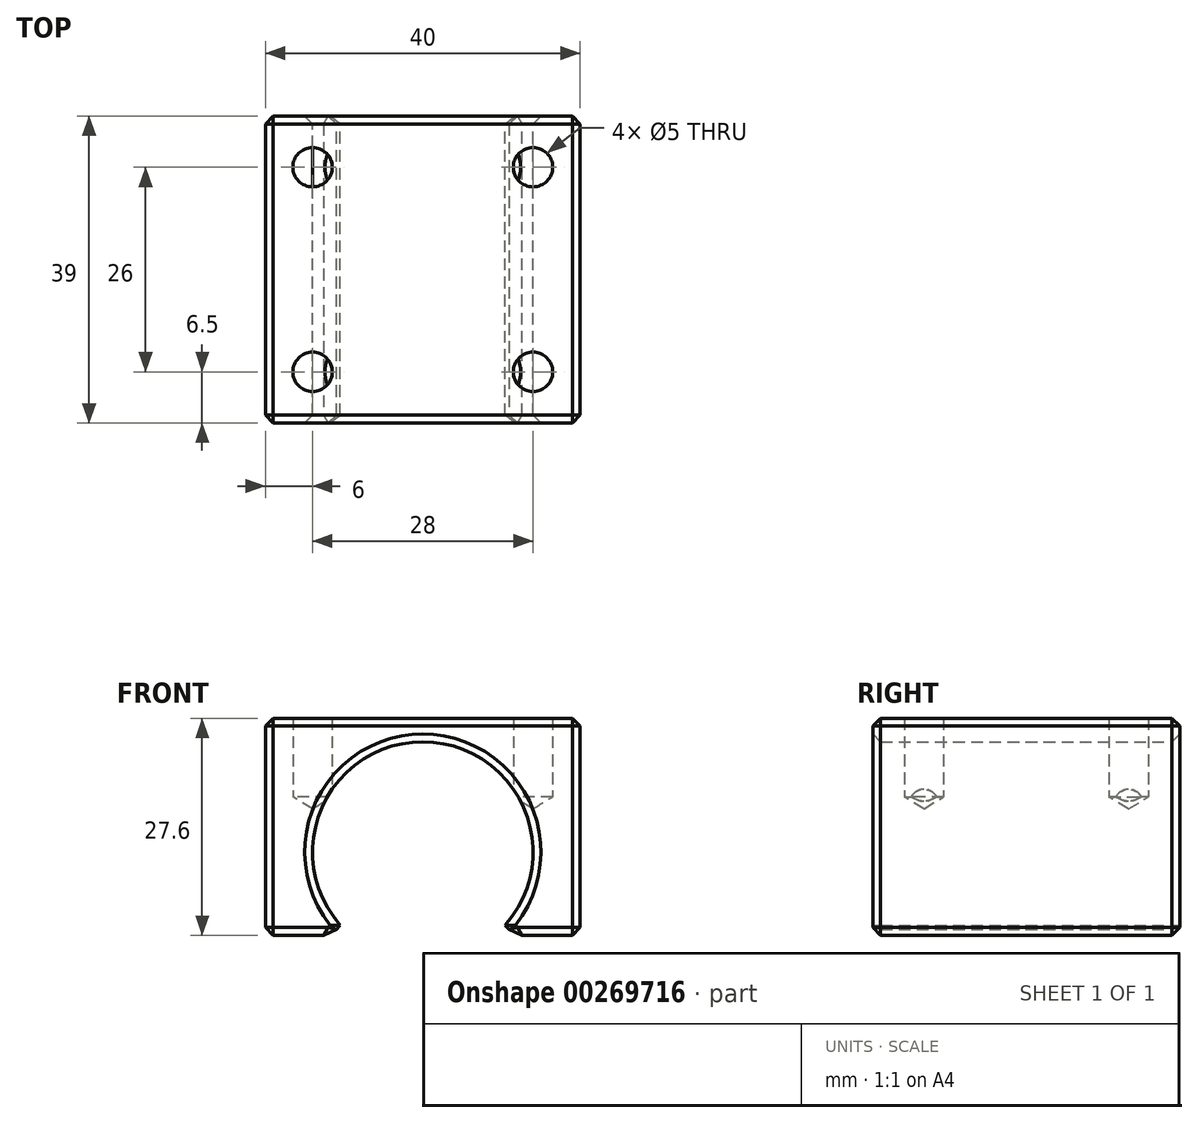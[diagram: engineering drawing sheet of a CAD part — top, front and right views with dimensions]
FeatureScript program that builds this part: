
annotation { "Feature Type Name" : "Feature", "Feature Type Description" : "" }
export const myFeature = defineFeature(function(context is Context, id is Id, definition is map)
    precondition{}
    {
        {
            var Q0;
            Q0=qCreatedBy(makeId("Front.planeOp"),FACE);
            var sketch = newSketch(context, id + "F0", { "sketchPlane" : qUnion([Q0])});
            skLineSegment(sketch, "E0.bottom", {"start": v(20, 13.8) * mm, "end": v(-20, 13.8) * mm});
            skLineSegment(sketch, "E0.top", {"start": v(20, -13.8) * mm, "end": v(11.58, -13.8) * mm});
            skLineSegment(sketch, "E0.left", {"start": v(20, 13.8) * mm, "end": v(20, -13.8) * mm});
            skLineSegment(sketch, "E0.right", {"start": v(-20, 13.8) * mm, "end": v(-20, -13.8) * mm});
            skPoint(sketch, "E0.middle", {"position": v(0, 0) * mm});
            skArc(sketch, "E1", {"start": v(10.48, -12.49) * mm, "mid": v(0, 10.8) * mm, "end": v(-10.48, -12.49) * mm});
            skLineSegment(sketch, "E2", {"start": v(-11.58, -13.8) * mm, "end": v(-10.48, -12.49) * mm});
            skLineSegment(sketch, "E3", {"start": v(11.58, -13.8) * mm, "end": v(10.48, -12.49) * mm});
            skLineSegment(sketch, "E4.trimOffspring", {"start": v(-11.58, -13.8) * mm, "end": v(-20, -13.8) * mm});
            skSolve(sketch);
        }
        {
            var Q0;
            Q0=makeQuery(id+"F0.imprint","IMPRINT",FACE,{"disambiguationData":[TD([[makeQuery(id+"F0.imprint","IMPRINT",EDGE,{"derivedFrom":sQuery(id+"F0.wireOp",EDGE,"E0.bottom")}),1.0]])]});
            extrude(context, id + "F1", {"entities" : qUnion([Q0]), "depth" : 39 * mm});
        }
        {
            var Q0;
            Q0=makeQuery(id+"F1.opExtrude","SWEPT_FACE",FACE,{"disambiguationData":[OSD([sQuery(id+"F0.wireOp",EDGE,"E0.bottom")])]});
            var sketch = newSketch(context, id + "F2", { "sketchPlane" : qUnion([Q0])});
            skPoint(sketch, "E5", {"position": v(-14, -6.5) * mm});
            skPoint(sketch, "E6", {"position": v(-14, -32.5) * mm});
            skPoint(sketch, "E7", {"position": v(14, -32.5) * mm});
            skPoint(sketch, "E8", {"position": v(14, -6.5) * mm});
            skLineSegment(sketch, "E9", {"start": v(-20, -19.5) * mm, "end": v(20, -19.5) * mm, "construction": true});
            skSolve(sketch);
        }
        {
            var Q0;
            Q0=sQuery(id+"F2.wireOp",VERTEX,"E5");
            var Q1;
            Q1=sQuery(id+"F2.wireOp",VERTEX,"E8");
            var Q2;
            Q2=sQuery(id+"F2.wireOp",VERTEX,"E7");
            var Q3;
            Q3=sQuery(id+"F2.wireOp",VERTEX,"E6");
            var Q4;
            Q4=makeQuery(id+"F1.opExtrude","SWEPT_BODY",BODY,{"disambiguationData":[OSD([sQuery(id+"F0.wireOp",EDGE,"E0.bottom"),sQuery(id+"F0.wireOp",EDGE,"E0.top"),sQuery(id+"F0.wireOp",EDGE,"E0.left"),sQuery(id+"F0.wireOp",EDGE,"E0.right"),sQuery(id+"F0.wireOp",EDGE,"E1"),sQuery(id+"F0.wireOp",EDGE,"E2"),sQuery(id+"F0.wireOp",EDGE,"E3"),sQuery(id+"F0.wireOp",EDGE,"E4.trimOffspring")])]});
            hole(context, id + "F3", {"style" : HoleStyle.SIMPLE, "endStyle" : HoleEndStyle.BLIND, "holeDiameter" : 5 * mm, "holeDepth" : 10 * mm, "locations" : qUnion([Q0, Q1, Q2, Q3]), "scope" : qUnion([Q4]), "startStyle" : HoleStartStyle.PART});
        }
        {
            var Q0;
            Q0=makeQuery(id+"F1.opExtrude","CAP_FACE",FACE,{"disambiguationData":[OSD([sQuery(id+"F0.wireOp",EDGE,"E0.bottom"),sQuery(id+"F0.wireOp",EDGE,"E0.top"),sQuery(id+"F0.wireOp",EDGE,"E0.left"),sQuery(id+"F0.wireOp",EDGE,"E0.right"),sQuery(id+"F0.wireOp",EDGE,"E1"),sQuery(id+"F0.wireOp",EDGE,"E2"),sQuery(id+"F0.wireOp",EDGE,"E3"),sQuery(id+"F0.wireOp",EDGE,"E4.trimOffspring")])],"isStart":true});
            var Q1;
            Q1=makeQuery(id+"F1.opExtrude","SWEPT_FACE",FACE,{"disambiguationData":[OSD([sQuery(id+"F0.wireOp",EDGE,"E0.right")])]});
            var Q2;
            Q2=makeQuery(id+"F1.opExtrude","CAP_FACE",FACE,{"disambiguationData":[OSD([sQuery(id+"F0.wireOp",EDGE,"E0.bottom"),sQuery(id+"F0.wireOp",EDGE,"E0.top"),sQuery(id+"F0.wireOp",EDGE,"E0.left"),sQuery(id+"F0.wireOp",EDGE,"E0.right"),sQuery(id+"F0.wireOp",EDGE,"E1"),sQuery(id+"F0.wireOp",EDGE,"E2"),sQuery(id+"F0.wireOp",EDGE,"E3"),sQuery(id+"F0.wireOp",EDGE,"E4.trimOffspring")])],"isStart":false});
            var Q3;
            Q3=makeQuery(id+"F1.opExtrude","SWEPT_FACE",FACE,{"disambiguationData":[OSD([sQuery(id+"F0.wireOp",EDGE,"E4.trimOffspring")])]});
            var Q4;
            Q4=makeQuery(id+"F1.opExtrude","SWEPT_FACE",FACE,{"disambiguationData":[OSD([sQuery(id+"F0.wireOp",EDGE,"E0.top")])]});
            var Q5;
            Q5=makeQuery(id+"F1.opExtrude","SWEPT_FACE",FACE,{"disambiguationData":[OSD([sQuery(id+"F0.wireOp",EDGE,"E0.left")])]});
            chamfer(context, id + "F4", {"entities" : qUnion([Q0, Q1, Q2, Q3, Q4, Q5]), "width" : 1 * mm, "tangentPropagation" : true});
        }
    });
